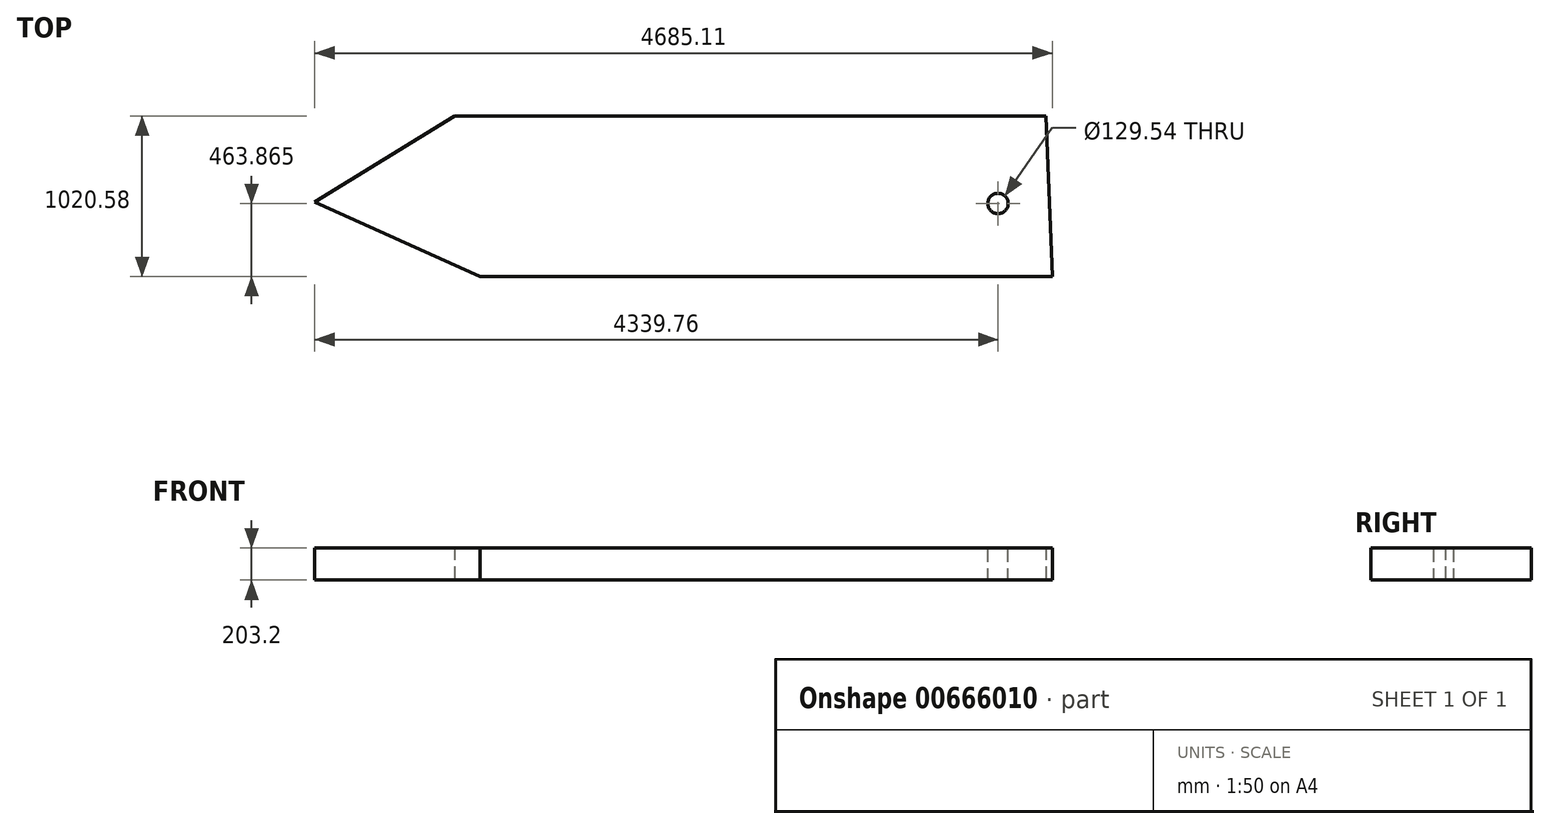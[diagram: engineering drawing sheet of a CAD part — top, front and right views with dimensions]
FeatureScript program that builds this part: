
annotation { "Feature Type Name" : "Feature", "Feature Type Description" : "" }
export const myFeature = defineFeature(function(context is Context, id is Id, definition is map)
    precondition{}
    {
        {
            var Q0;
            Q0=qCreatedBy(makeId("Top.planeOp"),FACE);
            var sketch = newSketch(context, id + "F0", { "sketchPlane" : qUnion([Q0])});
            skLineSegment(sketch, "E0", {"start": v(2707.93, -1451.03) * mm, "end": v(-927.1, -1451.03) * mm});
            skLineSegment(sketch, "E1", {"start": v(-927.1, -1451.03) * mm, "end": v(-1977.18, -978.25) * mm});
            skLineSegment(sketch, "E2", {"start": v(-1977.18, -978.25) * mm, "end": v(-1089.46, -430.45) * mm});
            skLineSegment(sketch, "E3", {"start": v(-1089.46, -430.45) * mm, "end": v(2668.9, -430.45) * mm});
            skLineSegment(sketch, "E4", {"start": v(2668.9, -430.45) * mm, "end": v(2707.93, -1451.03) * mm});
            skSolve(sketch);
        }
        {
            var Q0;
            Q0=makeQuery(id+"F0.imprint","IMPRINT",FACE,{"disambiguationData":[TD([[makeQuery(id+"F0.imprint","IMPRINT",EDGE,{"derivedFrom":sQuery(id+"F0.wireOp",EDGE,"E0")}),-1.0]])]});
            extrude(context, id + "F1", {"entities" : qUnion([Q0]), "depth" : 203.2 * mm, "offsetDistance" : 25.4 * mm});
        }
        {
            var Q0;
            Q0=makeQuery(id+"F1.opExtrude","CAP_FACE",FACE,{"disambiguationData":[OSD([sQuery(id+"F0.wireOp",EDGE,"E0"),sQuery(id+"F0.wireOp",EDGE,"E1"),sQuery(id+"F0.wireOp",EDGE,"E2"),sQuery(id+"F0.wireOp",EDGE,"E3"),sQuery(id+"F0.wireOp",EDGE,"E4")])],"isStart":false});
            var sketch = newSketch(context, id + "F2", { "sketchPlane" : qUnion([Q0])});
            skCircle(sketch, "E5", {"center": v(2362.58, -987.16) * mm, "radius": 64.77 * mm});
            skSolve(sketch);
        }
        {
            var Q0;
            Q0 = qSketchRegion(id + "F2", true);
            extrude(context, id + "F3", {"entities" : qUnion([Q0]), "operationType" : NewBodyOperationType.REMOVE, "endBound" : BoundingType.THROUGH_ALL, "oppositeDirection" : true, "depth" : 25.4 * mm, "offsetDistance" : 25.4 * mm});
        }
    });
